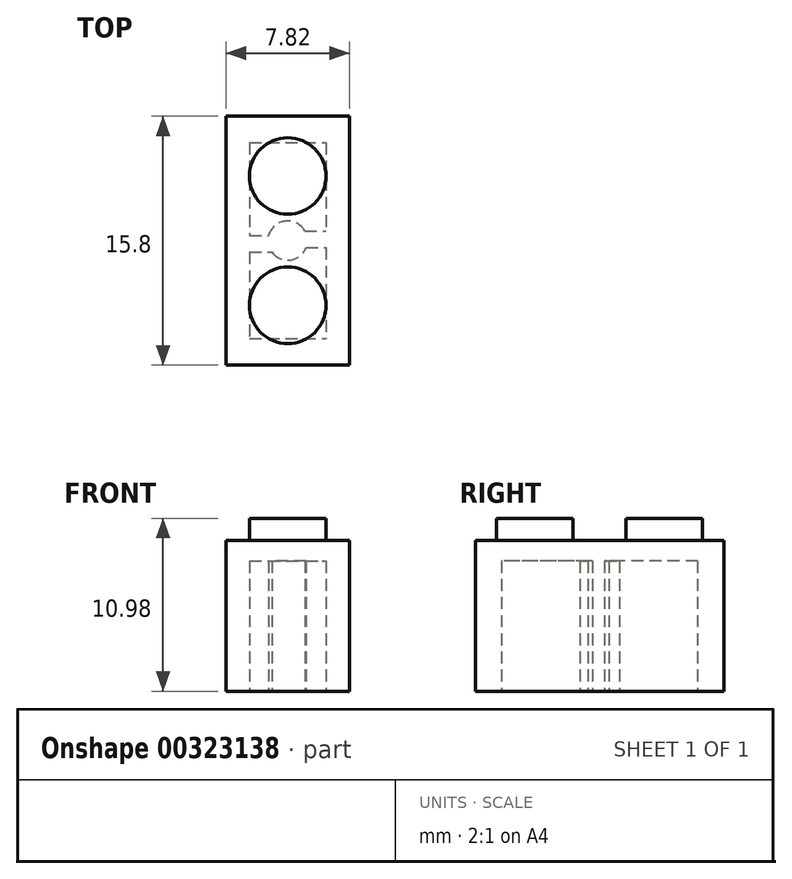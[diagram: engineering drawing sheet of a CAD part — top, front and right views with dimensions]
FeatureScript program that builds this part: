
annotation { "Feature Type Name" : "Feature", "Feature Type Description" : "" }
export const myFeature = defineFeature(function(context is Context, id is Id, definition is map)
    precondition{}
    {
        {
            var Q0;
            Q0=qCreatedBy(makeId("Top.planeOp"),FACE);
            var sketch = newSketch(context, id + "F0", { "sketchPlane" : qUnion([Q0])});
            skLineSegment(sketch, "E0.bottom", {"start": v(-3.91, 7.9) * mm, "end": v(3.91, 7.9) * mm});
            skLineSegment(sketch, "E0.top", {"start": v(-3.91, -7.9) * mm, "end": v(3.9, -7.9) * mm});
            skLineSegment(sketch, "E0.left", {"start": v(-3.91, 7.9) * mm, "end": v(-3.91, -7.9) * mm});
            skLineSegment(sketch, "E0.right", {"start": v(3.91, 7.9) * mm, "end": v(3.9, -7.9) * mm});
            skPoint(sketch, "E0.middle", {"position": v(0, 0) * mm});
            skCircle(sketch, "E1", {"center": v(0, -4.11) * mm, "radius": 2.43 * mm});
            skCircle(sketch, "E2", {"center": v(0, 4.1) * mm, "radius": 2.43 * mm});
            skSolve(sketch);
        }
        {
            var Q0;
            Q0 = qSketchRegion(id + "F0", true);
            var Q1;
            Q1=makeQuery(id+"F0.imprint","IMPRINT",FACE,{"disambiguationData":[TD([[makeQuery(id+"F0.imprint","IMPRINT",EDGE,{"derivedFrom":sQuery(id+"F0.wireOp",EDGE,"E1")}),1.0]])]});
            var Q2;
            Q2=makeQuery(id+"F0.imprint","IMPRINT",FACE,{"disambiguationData":[TD([[makeQuery(id+"F0.imprint","IMPRINT",EDGE,{"derivedFrom":sQuery(id+"F0.wireOp",EDGE,"E2")}),1.0]])]});
            extrude(context, id + "F1", {"entities" : qUnion([Q0, Q1, Q2]), "depth" : 9.58 * mm});
        }
        {
            var Q0;
            Q0=makeQuery(id+"F0.imprint","IMPRINT",FACE,{"disambiguationData":[TD([[makeQuery(id+"F0.imprint","IMPRINT",EDGE,{"derivedFrom":sQuery(id+"F0.wireOp",EDGE,"E1")}),1.0]])]});
            var Q1;
            Q1=makeQuery(id+"F0.imprint","IMPRINT",FACE,{"disambiguationData":[TD([[makeQuery(id+"F0.imprint","IMPRINT",EDGE,{"derivedFrom":sQuery(id+"F0.wireOp",EDGE,"E2")}),1.0]])]});
            extrude(context, id + "F2", {"entities" : qUnion([Q0, Q1]), "operationType" : NewBodyOperationType.ADD, "depth" : 10.98 * mm});
        }
        {
            var Q0;
            Q0=makeQuery(id+"F1.opExtrude","CAP_FACE",FACE,{"disambiguationData":[OSD([sQuery(id+"F0.wireOp",EDGE,"E0.bottom"),sQuery(id+"F0.wireOp",EDGE,"E0.top"),sQuery(id+"F0.wireOp",EDGE,"E0.left"),sQuery(id+"F0.wireOp",EDGE,"E0.right")])],"isStart":true});
            var sketch = newSketch(context, id + "F3", { "sketchPlane" : qUnion([Q0])});
            skLineSegment(sketch, "E3.bottom", {"start": v(-2.43, -6.22) * mm, "end": v(2.43, -6.22) * mm});
            skLineSegment(sketch, "E3.top", {"start": v(-2.43, 6.22) * mm, "end": v(2.43, 6.22) * mm});
            skLineSegment(sketch, "E3.left", {"start": v(-2.43, -6.22) * mm, "end": v(-2.43, 6.22) * mm});
            skLineSegment(sketch, "E3.right", {"start": v(2.43, -6.22) * mm, "end": v(2.43, 6.22) * mm});
            skCircle(sketch, "E4", {"center": v(0, 0) * mm, "radius": 1.25 * mm});
            skLineSegment(sketch, "E5", {"start": v(-2.43, -0.32) * mm, "end": v(-1.2, -0.32) * mm});
            skLineSegment(sketch, "E6", {"start": v(-2.43, 0.74) * mm, "end": v(-1, 0.74) * mm});
            skLineSegment(sketch, "E7", {"start": v(1.16, 0.45) * mm, "end": v(2.43, 0.45) * mm});
            skLineSegment(sketch, "E8", {"start": v(1.09, -0.6) * mm, "end": v(2.43, -0.6) * mm});
            skSolve(sketch);
        }
        {
            var Q0;
            {var subQ1=sQuery(id+"F3.wireOp",EDGE,"E3.bottom");Q0=makeQuery(id+"F3.imprint","IMPRINT",FACE,{"disambiguationData":[TD([[makeQuery(id+"F3.imprint","IMPRINT",EDGE,{"derivedFrom":subQ1}),1.0]])]});}
            var Q1;
            {var subQ4=sQuery(id+"F3.wireOp",EDGE,"E3.top");Q1=makeQuery(id+"F3.imprint","IMPRINT",FACE,{"disambiguationData":[TD([[makeQuery(id+"F3.imprint","IMPRINT",EDGE,{"derivedFrom":subQ4}),-1.0]])]});}
            extrude(context, id + "F4", {"entities" : qUnion([Q0, Q1]), "operationType" : NewBodyOperationType.REMOVE, "oppositeDirection" : true, "depth" : 8.28 * mm});
        }
    });
